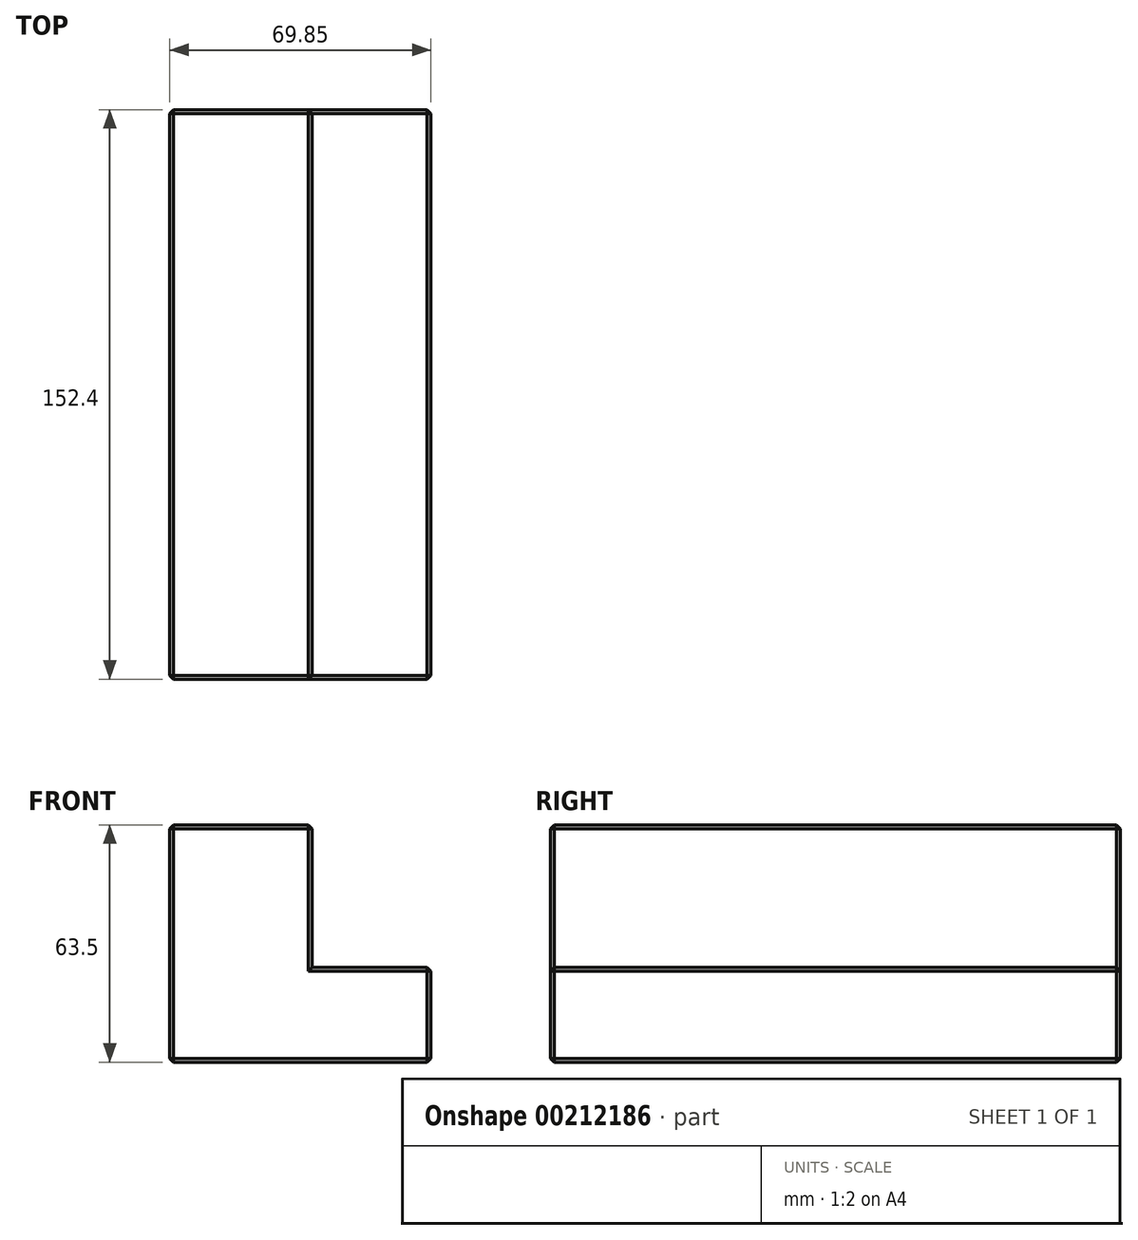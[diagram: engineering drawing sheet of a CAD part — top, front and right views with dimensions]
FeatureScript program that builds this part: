
annotation { "Feature Type Name" : "Feature", "Feature Type Description" : "" }
export const myFeature = defineFeature(function(context is Context, id is Id, definition is map)
    precondition{}
    {
        {
            var Q0;
            Q0=qCreatedBy(makeId("Front.planeOp"),FACE);
            var sketch = newSketch(context, id + "F0", { "sketchPlane" : qUnion([Q0])});
            skLineSegment(sketch, "E0", {"start": v(0, 0) * mm, "end": v(0, 63.5) * mm});
            skLineSegment(sketch, "E1", {"start": v(0, 63.5) * mm, "end": v(38.1, 63.5) * mm});
            skLineSegment(sketch, "E2", {"start": v(38.1, 63.5) * mm, "end": v(38.1, 25.4) * mm});
            skLineSegment(sketch, "E3", {"start": v(38.1, 25.4) * mm, "end": v(69.85, 25.4) * mm});
            skLineSegment(sketch, "E4", {"start": v(69.85, 25.4) * mm, "end": v(69.85, 0) * mm});
            skLineSegment(sketch, "E5", {"start": v(69.85, 0) * mm, "end": v(0, 0) * mm});
            skSolve(sketch);
        }
        {
            var Q0;
            Q0=makeQuery(id+"F0.imprint","IMPRINT",FACE,{"disambiguationData":[TD([[makeQuery(id+"F0.imprint","IMPRINT",EDGE,{"derivedFrom":sQuery(id+"F0.wireOp",EDGE,"E0")}),-1.0]])]});
            extrude(context, id + "F1", {"entities" : qUnion([Q0]), "depth" : 152.4 * mm});
        }
        {
            var Q0;
            Q0=makeQuery(id+"F1.opExtrude","SWEPT_FACE",FACE,{"disambiguationData":[OSD([sQuery(id+"F0.wireOp",EDGE,"E1")])]});
            var sketch = newSketch(context, id + "F2", { "sketchPlane" : qUnion([Q0])});
            skCircle(sketch, "E6", {"center": v(17.7, -28.58) * mm, "radius": 8 * mm});
            skCircle(sketch, "E7", {"center": v(17.7, -76.2) * mm, "radius": 8 * mm});
            skCircle(sketch, "E8", {"center": v(17.7, -123.83) * mm, "radius": 8 * mm});
            skSolve(sketch);
        }
        {
            var Q0;
            Q0=makeQuery(id+"F1.opExtrude","CAP_FACE",FACE,{"disambiguationData":[OSD([sQuery(id+"F0.wireOp",EDGE,"E0"),sQuery(id+"F0.wireOp",EDGE,"E1"),sQuery(id+"F0.wireOp",EDGE,"E2"),sQuery(id+"F0.wireOp",EDGE,"E3"),sQuery(id+"F0.wireOp",EDGE,"E4"),sQuery(id+"F0.wireOp",EDGE,"E5")])],"isStart":false});
            var Q1;
            Q1=makeQuery(id+"F1.opExtrude","CAP_FACE",FACE,{"disambiguationData":[OSD([sQuery(id+"F0.wireOp",EDGE,"E0"),sQuery(id+"F0.wireOp",EDGE,"E1"),sQuery(id+"F0.wireOp",EDGE,"E2"),sQuery(id+"F0.wireOp",EDGE,"E3"),sQuery(id+"F0.wireOp",EDGE,"E4"),sQuery(id+"F0.wireOp",EDGE,"E5")])],"isStart":true});
            var Q2;
            Q2=makeQuery(id+"F1.opExtrude","SWEPT_FACE",FACE,{"disambiguationData":[OSD([sQuery(id+"F0.wireOp",EDGE,"E1")])]});
            var Q3;
            Q3=makeQuery(id+"F1.opExtrude","SWEPT_FACE",FACE,{"disambiguationData":[OSD([sQuery(id+"F0.wireOp",EDGE,"E4")])]});
            var Q4;
            Q4=makeQuery(id+"F1.opExtrude","SWEPT_EDGE",EDGE,{"disambiguationData":[OSD([sQuery(id+"F0.wireOp",EDGE,"E0"),sQuery(id+"F0.wireOp",EDGE,"E5")])]});
            var Q5;
            Q5=makeQuery(id+"FJqBUw6U1LacLB2_1.boolean.opBoolean","INTERSECT",EDGE,{"derivedFrom":[makeQuery(id+"F1.opExtrude","SWEPT_FACE",FACE,{"disambiguationData":[OSD([sQuery(id+"F0.wireOp",EDGE,"E5")])]}),makeQuery(id+"FJqBUw6U1LacLB2_1.opExtrude","SWEPT_FACE",FACE,{"disambiguationData":[OSD([sQuery(id+"F2.wireOp",EDGE,"E8")])]})]});
            var Q6;
            Q6=makeQuery(id+"FJqBUw6U1LacLB2_1.boolean.opBoolean","INTERSECT",EDGE,{"derivedFrom":[makeQuery(id+"F1.opExtrude","SWEPT_FACE",FACE,{"disambiguationData":[OSD([sQuery(id+"F0.wireOp",EDGE,"E5")])]}),makeQuery(id+"FJqBUw6U1LacLB2_1.opExtrude","SWEPT_FACE",FACE,{"disambiguationData":[OSD([sQuery(id+"F2.wireOp",EDGE,"E7")])]})]});
            var Q7;
            Q7=makeQuery(id+"FJqBUw6U1LacLB2_1.boolean.opBoolean","INTERSECT",EDGE,{"derivedFrom":[makeQuery(id+"F1.opExtrude","SWEPT_FACE",FACE,{"disambiguationData":[OSD([sQuery(id+"F0.wireOp",EDGE,"E5")])]}),makeQuery(id+"FJqBUw6U1LacLB2_1.opExtrude","SWEPT_FACE",FACE,{"disambiguationData":[OSD([sQuery(id+"F2.wireOp",EDGE,"E6")])]})]});
            chamfer(context, id + "F3", {"entities" : qUnion([Q0, Q1, Q2, Q3, Q4, Q5, Q6, Q7]), "width" : 1.02 * mm, "tangentPropagation" : true});
        }
    });
